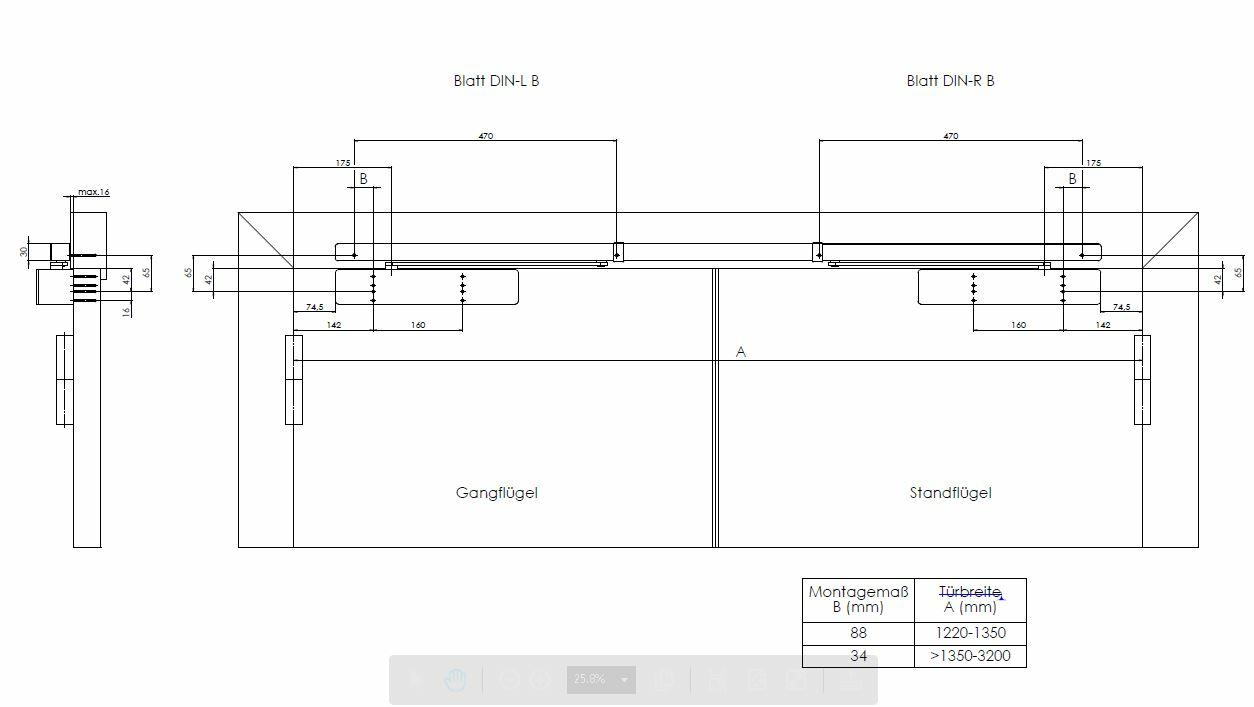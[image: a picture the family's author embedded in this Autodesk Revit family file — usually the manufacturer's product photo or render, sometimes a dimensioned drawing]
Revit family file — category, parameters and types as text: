
# Revit family: Doors - Hardware_Double-Door_Dormakaba_TS98-GSR-XEA
name_source: partatom
category: Allgemeines Modell
revit_build: Autodesk Revit 2016 (Build: 20150220_1215(x64)
units: mm (PartAtom-declared; Revit-internal decimal feet)

## family parameters
Basisbauteil = Fläche
Beim Laden mit Abzugskörper schneiden = Nein
Bemaßung runder Anschluss = Durchmesser verwenden
Gemeinsam genutzt = Nein
Kann Basisbauteil für Bewehrung sein = Nein
OmniClass-Nummer = 23.30.40.11.27.11
OmniClass-Titel = Door Closers
Raumberechnungspunkt = Nein
Teiletyp = Normal

## types (1)
- Doors - Hardware_Double-Door_Dormakaba_TS98-GSR-XEA
    Brand url = http://www.dormakaba.com
    Depth Jamb to Door = 0 mm  [stored 0 ft]
    Design country = Germany
    Door Closers Types = TS 98-GSR-XEA-Pull-Side-Door_Fixing
    Edition number = 1
    Extension Height = 17 mm
    Hinge Distance = 1800 mm  [stored 5.90551 ft]
    Manufacturer country = Germany
    Manufacturer name = DORMA
    Material main = Aluminium
    Material secondary = Zink
    Max Depth Jamb to Door = 0 mm  [stored 0 ft]
    NBS Reference Code = 25-38-20-20
    NBS Reference Description = Door Hardware Systems
    Nominal height = 30 mm  [stored 0.0984252 ft]
    Nominal width = 3051 mm  [stored 10.0098 ft]
    OmniClass Code = 23-17 19 11 19 11
    OmniClass Description = Door Closers
    Opening Angle = 0.00°
    Primary Material = Aluminium-Dormakaba-Anodized Silver
    Product SKU = g-sr_xea
    Product url = http://www.dorma.com
    Pull Side Door = TS 98-GSR-XEA-Pull-Side-Door_Fixing
    Push side = TS 98-GSR-XEA_Push-Side-Door_Fixing
    Uniclass 1.4 Code = L41812
    Uniclass 1.4 Description = Door closers
    Uniclass 2015 Code = Pr_30_36_59_92
    Uniclass 2015 Name = Uncontrolled door closers
    Vorgabe-Ansicht = 1219 mm
    Weight Net (Kg) = 3.4

note: [stored X ft] marks values corroborated as IEEE doubles in the binary element streams (Revit-internal decimal feet)

## geometry (parser evidence)
native form markers: Blend x2, Sweep x17
no freeform markers — native parametric forms only
